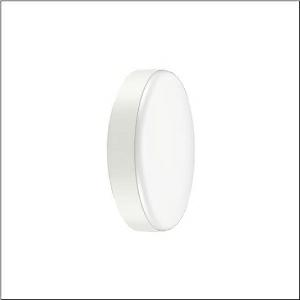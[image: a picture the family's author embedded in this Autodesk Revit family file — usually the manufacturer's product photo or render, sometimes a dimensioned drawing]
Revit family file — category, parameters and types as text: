
# Revit family: rondel_31_51wc10db44a
name_source: partatom
category: Lighting Fixtures
units: mm (PartAtom-declared; Revit-internal decimal feet)

## family parameters
Cut with Voids When Loaded = No
Host = Face
Light Source = No
Part Type = Normal
Room Calculation Point = No
Round Connector Dimension = Use Diameter
Shared = No

## types (1)
- Rondel 31 (1 x LED, 4400 lm, 34 W, 4000K)
    Apparent Load = 34 VA
    CIE Flux Codes = 44 75 94 94 100
    Color Rendering = 80
    Color Temperature = 4000K
    Default Elevation = 1800 mm
    Description = Rondel 31, wall and ceiling luminaire, primary optical cover: cover, of PC, opal, light emission: direct distribution, primary light characteristic: symmetric, installation type: surface-mounted, LED, rated luminous flux: 4.250lm, luminous efficacy: 125lm/W, light colour: 840, colour temperature: 4000K, with terminal, 3-pole, max. 2.5mm², mains connection: 220..240V, AC, 50/60Hz, rated input power: 34W, luminaire housing, of PC, traffic white (RAL 9016), diameter: 480mm, protection rating (complete): IP65, insulation class (complete): insulation class II (safety insulation), certification: CE, impact resistance: IK10, permissible storage temperature: -20..+60°C, packaging unit: 1 piece
    Height = 97 mm
    Lamp = 1 x LED
    Lamp Light Flux = 4400 lm
    Lamp Power = 34 W
    Lamp count = 1
    Length = 480 mm
    Luminous efficacy = 129 lm/W
    Manufacturer = Siteco
    ModVariant = No
    Model = 51WC10DB44A
    Mounting Place = Ceiling
    Mounting Type = Surface mounted
    Number of Poles = 1
    OnlyDefault = Yes
    Power Factor = 1
    Product Name = Rondel 31
    Product group = wall and ceiling luminaire
    ProductGroupID = 301
    Protection Class = Protection class II
    Protection Degree = IP 65
    RLX_Detail_Level = 1
    RlxData = <blob elided: 40641 chars, md5=fe087f5b>
    Socket = socket
    Standby Power = 0 W
    System Light Flux = 4400 lm
    System Power = 34 W
    Type Comments = Product without accessories
    Type Image = l_1007188.jpg
    URL = http://relux.com
    VarID = ---
    Voltage = 0 V
    Weight = 0.00 kg
    Width = 0 mm  [stored 0 ft]

note: [stored X ft] marks values corroborated as IEEE doubles in the binary element streams (Revit-internal decimal feet)

## geometry (parser evidence)
native form markers: Blend x4, Sweep x12
no freeform markers — native parametric forms only
